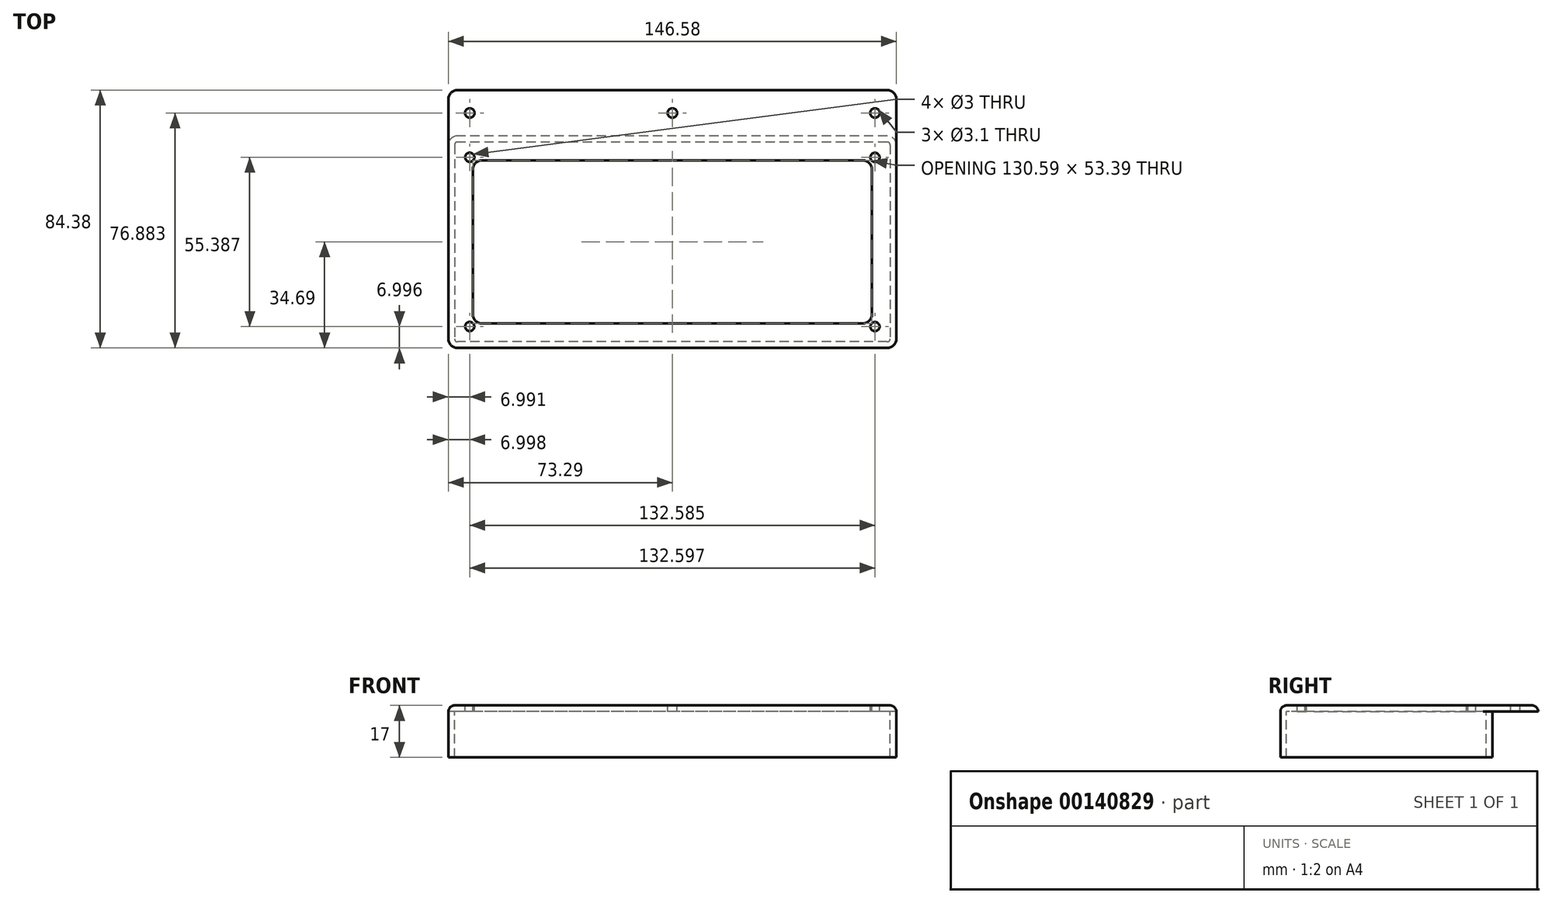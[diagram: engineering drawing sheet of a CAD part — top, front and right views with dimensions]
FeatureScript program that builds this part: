
annotation { "Feature Type Name" : "Feature", "Feature Type Description" : "" }
export const myFeature = defineFeature(function(context is Context, id is Id, definition is map)
    precondition{}
    {
        {
            var Q0;
            Q0=qCreatedBy(makeId("Top.planeOp"),FACE);
            var sketch = newSketch(context, id + "F0", { "sketchPlane" : qUnion([Q0])});
            skCircle(sketch, "E0.0", {"center": v(-66.3, 27.7) * mm, "radius": 2 * mm});
            skCircle(sketch, "E0.2", {"center": v(66.3, -27.7) * mm, "radius": 2 * mm});
            skCircle(sketch, "E0.3", {"center": v(-66.3, -27.68) * mm, "radius": 2 * mm});
            skCircle(sketch, "E1.0", {"center": v(66.3, 27.68) * mm, "radius": 2 * mm});
            skLineSegment(sketch, "E2.0", {"start": v(-69.85, 28.07) * mm, "end": v(-69.85, -28.06) * mm});
            skArc(sketch, "E2.1", {"start": v(-66.67, 31.25) * mm, "mid": v(-68.92, 30.32) * mm, "end": v(-69.85, 28.07) * mm});
            skLineSegment(sketch, "E2.2", {"start": v(66.68, 31.23) * mm, "end": v(-66.67, 31.25) * mm});
            skArc(sketch, "E2.3", {"start": v(69.85, 28.06) * mm, "mid": v(68.92, 30.3) * mm, "end": v(66.68, 31.23) * mm});
            skLineSegment(sketch, "E2.4", {"start": v(69.85, -28.08) * mm, "end": v(69.85, 28.06) * mm});
            skArc(sketch, "E2.5", {"start": v(66.67, -31.25) * mm, "mid": v(68.92, -30.32) * mm, "end": v(69.85, -28.08) * mm});
            skLineSegment(sketch, "E2.6", {"start": v(-66.68, -31.24) * mm, "end": v(66.67, -31.25) * mm});
            skArc(sketch, "E2.7", {"start": v(-69.85, -28.06) * mm, "mid": v(-68.92, -30.3) * mm, "end": v(-66.68, -31.24) * mm});
            skSolve(sketch);
        }
        {
            var Q0;
            Q0=qCreatedBy(makeId("Top.planeOp"),FACE);
            var sketch = newSketch(context, id + "F1", { "sketchPlane" : qUnion([Q0])});
            skLineSegment(sketch, "E3.bottom", {"start": v(70.3, 34.7) * mm, "end": v(-70.3, 34.7) * mm});
            skLineSegment(sketch, "E3.top", {"start": v(70.3, -34.7) * mm, "end": v(-70.3, -34.7) * mm});
            skLineSegment(sketch, "E3.left", {"start": v(73.3, 31.7) * mm, "end": v(73.3, -31.7) * mm});
            skLineSegment(sketch, "E3.right", {"start": v(-73.3, 31.7) * mm, "end": v(-73.3, -31.7) * mm});
            skPoint(sketch, "E3.middle", {"position": v(0, 0) * mm});
            skLineSegment(sketch, "E4.bottom", {"start": v(62.3, -26.7) * mm, "end": v(-62.3, -26.7) * mm});
            skLineSegment(sketch, "E4.top", {"start": v(62.3, 26.7) * mm, "end": v(-62.3, 26.7) * mm});
            skLineSegment(sketch, "E4.left", {"start": v(65.3, -23.7) * mm, "end": v(65.3, 23.7) * mm});
            skLineSegment(sketch, "E4.right", {"start": v(-65.3, -23.7) * mm, "end": v(-65.3, 23.7) * mm});
            skLineSegment(sketch, "E5", {"start": v(-73.3, 34.7) * mm, "end": v(-73.3, 46.7) * mm});
            skLineSegment(sketch, "E6", {"start": v(-70.3, 49.7) * mm, "end": v(70.3, 49.7) * mm});
            skLineSegment(sketch, "E7", {"start": v(73.3, 46.7) * mm, "end": v(73.3, 34.7) * mm});
            skCircle(sketch, "E8", {"center": v(0, 42.2) * mm, "radius": 1.55 * mm});
            skPoint(sketch, "E8.centerSnap0", {"position": v(-73.3, 42.2) * mm});
            skPoint(sketch, "E8.centerSnap1", {"position": v(0, 49.7) * mm});
            skCircle(sketch, "E9", {"center": v(-66.3, 42.2) * mm, "radius": 1.55 * mm});
            skCircle(sketch, "E10.MirrorC", {"center": v(66.3, 42.2) * mm, "radius": 1.55 * mm});
            skPoint(sketch, "E11.visualSharp", {"position": v(-73.3, -34.7) * mm});
            skArc(sketch, "E11.filletArc", {"start": v(-73.3, -31.7) * mm, "mid": v(-72.41, -33.81) * mm, "end": v(-70.3, -34.7) * mm});
            skPoint(sketch, "E12.visualSharp", {"position": v(-73.3, 49.7) * mm});
            skArc(sketch, "E12.filletArc", {"start": v(-70.3, 49.7) * mm, "mid": v(-72.41, 48.81) * mm, "end": v(-73.3, 46.7) * mm});
            skPoint(sketch, "E13.visualSharp", {"position": v(73.3, 49.7) * mm});
            skArc(sketch, "E13.filletArc", {"start": v(73.3, 46.7) * mm, "mid": v(72.41, 48.81) * mm, "end": v(70.3, 49.7) * mm});
            skPoint(sketch, "E14.visualSharp", {"position": v(73.3, -34.7) * mm});
            skArc(sketch, "E14.filletArc", {"start": v(70.3, -34.7) * mm, "mid": v(72.41, -33.81) * mm, "end": v(73.3, -31.7) * mm});
            skPoint(sketch, "E15.visualSharp", {"position": v(-65.3, -26.7) * mm});
            skArc(sketch, "E15.filletArc", {"start": v(-65.3, -23.7) * mm, "mid": v(-64.41, -25.81) * mm, "end": v(-62.3, -26.7) * mm});
            skPoint(sketch, "E16.visualSharp", {"position": v(-65.3, 26.7) * mm});
            skArc(sketch, "E16.filletArc", {"start": v(-62.3, 26.7) * mm, "mid": v(-64.41, 25.81) * mm, "end": v(-65.3, 23.7) * mm});
            skPoint(sketch, "E17.visualSharp", {"position": v(65.3, 26.7) * mm});
            skArc(sketch, "E17.filletArc", {"start": v(65.3, 23.7) * mm, "mid": v(64.41, 25.81) * mm, "end": v(62.3, 26.7) * mm});
            skPoint(sketch, "E18.visualSharp", {"position": v(65.3, -26.7) * mm});
            skArc(sketch, "E18.filletArc", {"start": v(62.3, -26.7) * mm, "mid": v(64.41, -25.81) * mm, "end": v(65.3, -23.7) * mm});
            skPoint(sketch, "E19.visualSharp", {"position": v(73.3, 34.7) * mm});
            skArc(sketch, "E19.filletArc", {"start": v(73.3, 31.7) * mm, "mid": v(72.41, 33.81) * mm, "end": v(70.3, 34.7) * mm});
            skPoint(sketch, "E20.visualSharp", {"position": v(-73.3, 34.7) * mm});
            skArc(sketch, "E20.filletArc", {"start": v(-70.3, 34.7) * mm, "mid": v(-72.41, 33.81) * mm, "end": v(-73.3, 31.7) * mm});
            skLineSegment(sketch, "E21", {"start": v(-73.3, 31.7) * mm, "end": v(-73.3, 34.7) * mm});
            skLineSegment(sketch, "E22", {"start": v(73.3, 34.7) * mm, "end": v(73.3, 31.7) * mm});
            skSolve(sketch);
        }
        {
            var Q0;
            Q0=makeQuery(id+"F1.imprint","IMPRINT",FACE,{"disambiguationData":[TD([[makeQuery(id+"F1.imprint","IMPRINT",EDGE,{"derivedFrom":sQuery(id+"F1.wireOp",EDGE,"E3.bottom")}),1.0]])]});
            var Q1;
            Q1=makeQuery(id+"F1.imprint","IMPRINT",FACE,{"disambiguationData":[TD([[makeQuery(id+"F1.imprint","IMPRINT",EDGE,{"derivedFrom":sQuery(id+"F1.wireOp",EDGE,"E4.bottom")}),-1.0]])]});
            extrude(context, id + "F2", {"entities" : qUnion([Q0, Q1]), "oppositeDirection" : true, "depth" : 17 * mm});
        }
        {
            var Q0;
            Q0=makeQuery(id+"F2.opExtrude","CAP_FACE",FACE,{"disambiguationData":[OSD([sQuery(id+"F1.wireOp",EDGE,"E3.bottom"),sQuery(id+"F1.wireOp",EDGE,"E3.top"),sQuery(id+"F1.wireOp",EDGE,"E3.left"),sQuery(id+"F1.wireOp",EDGE,"E3.right"),sQuery(id+"F1.wireOp",EDGE,"E11.filletArc"),sQuery(id+"F1.wireOp",EDGE,"E14.filletArc"),sQuery(id+"F1.wireOp",EDGE,"E19.filletArc"),sQuery(id+"F1.wireOp",EDGE,"E20.filletArc")])],"isStart":false});
            shell(context, id + "F3", {"entities" : qUnion([Q0]), "thickness" : 2 * mm});
        }
        {
            var Q0;
            Q0=makeQuery(id+"F1.imprint","IMPRINT",FACE,{"disambiguationData":[TD([[makeQuery(id+"F1.imprint","IMPRINT",EDGE,{"derivedFrom":sQuery(id+"F1.wireOp",EDGE,"E3.bottom")}),-1.0]])]});
            extrude(context, id + "F4", {"entities" : qUnion([Q0]), "operationType" : NewBodyOperationType.ADD, "oppositeDirection" : true, "depth" : 2 * mm});
        }
        {
            var Q0;
            Q0=makeQuery(id+"F1.imprint","IMPRINT",FACE,{"disambiguationData":[TD([[makeQuery(id+"F1.imprint","IMPRINT",EDGE,{"derivedFrom":sQuery(id+"F1.wireOp",EDGE,"E4.bottom")}),-1.0]])]});
            extrude(context, id + "F5", {"entities" : qUnion([Q0]), "operationType" : NewBodyOperationType.REMOVE, "oppositeDirection" : true, "depth" : 25 * mm});
        }
        {
            var Q0;
            Q0=sQuery(id+"F0.wireOp",VERTEX,"E0.0.center");
            var Q1;
            Q1=sQuery(id+"F0.wireOp",VERTEX,"E1.0.center");
            var Q2;
            Q2=sQuery(id+"F0.wireOp",VERTEX,"E0.2.center");
            var Q3;
            Q3=sQuery(id+"F0.wireOp",VERTEX,"E0.3.center");
            var Q4;
            Q4=makeQuery(id+"F2.opExtrude","SWEPT_BODY",BODY,{"disambiguationData":[OSD([sQuery(id+"F1.wireOp",EDGE,"E3.bottom"),sQuery(id+"F1.wireOp",EDGE,"E3.top"),sQuery(id+"F1.wireOp",EDGE,"E3.left"),sQuery(id+"F1.wireOp",EDGE,"E3.right"),sQuery(id+"F1.wireOp",EDGE,"E11.filletArc"),sQuery(id+"F1.wireOp",EDGE,"E14.filletArc"),sQuery(id+"F1.wireOp",EDGE,"E19.filletArc"),sQuery(id+"F1.wireOp",EDGE,"E20.filletArc")])]});
            hole(context, id + "F6", {"style" : HoleStyle.SIMPLE, "endStyle" : HoleEndStyle.THROUGH, "holeDiameter" : 3 * mm, "locations" : qUnion([Q0, Q1, Q2, Q3]), "scope" : qUnion([Q4]), "isTappedThrough" : true});
        }
        {
            var Q0;
            Q0=makeQuery(id+"F4.boolean.opBoolean","MERGE",EDGE,{"derivedFrom":[makeQuery(id+"F2.opExtrude","CAP_EDGE",EDGE,{"disambiguationData":[OSD([sQuery(id+"F1.wireOp",EDGE,"E3.right")])],"isStart":true}),makeQuery(id+"F4.opExtrude","CAP_EDGE",EDGE,{"disambiguationData":[OSD([sQuery(id+"F1.wireOp",EDGE,"E5"),sQuery(id+"F1.wireOp",EDGE,"E21")])],"isStart":true})]});
            fillet(context, id + "F7", {"entities" : qUnion([Q0]), "radius" : 2 * mm, "tangentPropagation" : true, "allowEdgeOverflow" : false});
        }
    });
